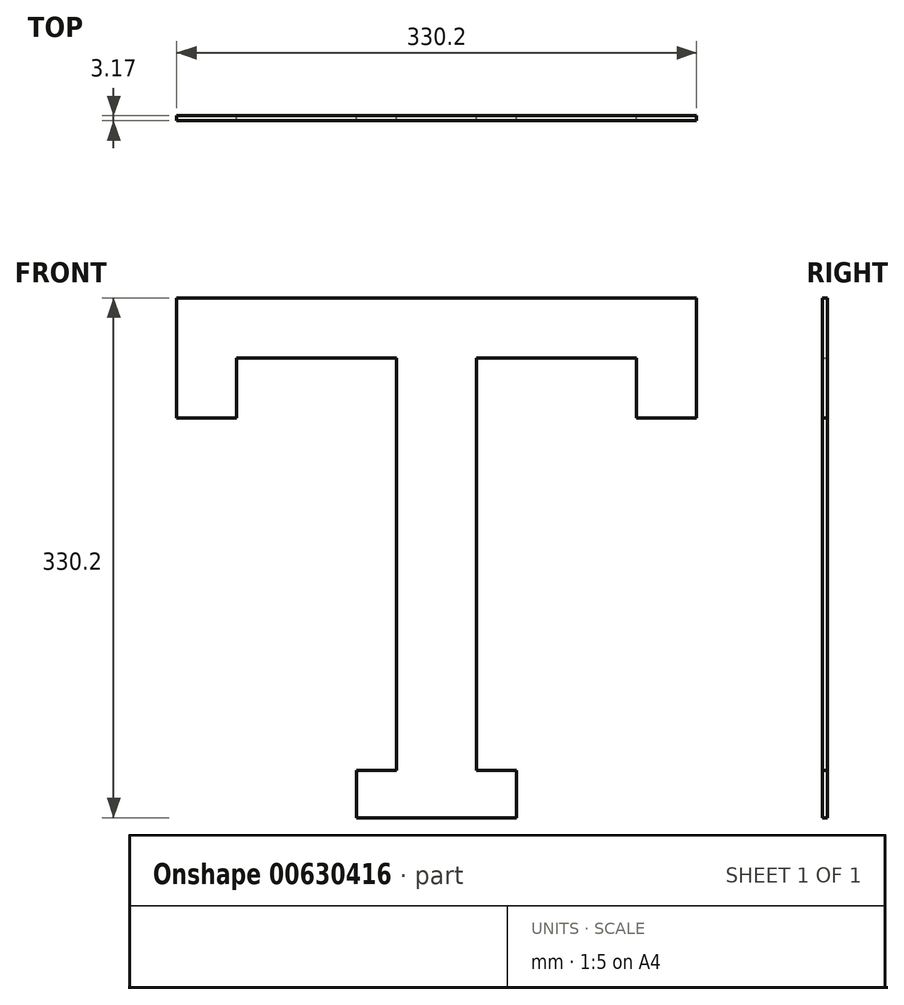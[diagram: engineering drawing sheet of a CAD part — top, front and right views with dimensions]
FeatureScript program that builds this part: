
annotation { "Feature Type Name" : "Feature", "Feature Type Description" : "" }
export const myFeature = defineFeature(function(context is Context, id is Id, definition is map)
    precondition{}
    {
        {
            var Q0;
            Q0=qCreatedBy(makeId("Front.planeOp"),FACE);
            var sketch = newSketch(context, id + "F0", { "sketchPlane" : qUnion([Q0])});
            skLineSegment(sketch, "E0.bottom", {"start": v(-25.4, 330.2) * mm, "end": v(0, 330.2) * mm});
            skLineSegment(sketch, "E0.top", {"start": v(-25.4, 0) * mm, "end": v(0, 0) * mm});
            skLineSegment(sketch, "E0.left", {"start": v(-25.4, 292.1) * mm, "end": v(-25.4, 30.02) * mm});
            skLineSegment(sketch, "E0.right", {"start": v(0, 330.2) * mm, "end": v(0, 0) * mm, "construction": true});
            skLineSegment(sketch, "E1.bottom", {"start": v(0, 330.2) * mm, "end": v(-165.1, 330.2) * mm});
            skLineSegment(sketch, "E1.top", {"start": v(-25.4, 292.1) * mm, "end": v(-127, 292.1) * mm});
            skLineSegment(sketch, "E1.left", {"start": v(0, 330.2) * mm, "end": v(0, 292.1) * mm});
            skLineSegment(sketch, "E1.right", {"start": v(-165.1, 330.2) * mm, "end": v(-165.1, 292.1) * mm});
            skLineSegment(sketch, "E2.bottom", {"start": v(-165.1, 330.2) * mm, "end": v(-127, 330.2) * mm});
            skLineSegment(sketch, "E2.top", {"start": v(-165.1, 254) * mm, "end": v(-127, 254) * mm});
            skLineSegment(sketch, "E2.left", {"start": v(-165.1, 330.2) * mm, "end": v(-165.1, 254) * mm});
            skLineSegment(sketch, "E2.right", {"start": v(-127, 292.1) * mm, "end": v(-127, 254) * mm});
            skLineSegment(sketch, "E3.bottom", {"start": v(0, 0) * mm, "end": v(-50.8, 0) * mm});
            skLineSegment(sketch, "E3.top", {"start": v(-25.4, 30.02) * mm, "end": v(-50.8, 30.02) * mm});
            skLineSegment(sketch, "E3.left", {"start": v(0, 0) * mm, "end": v(0, 30.02) * mm});
            skLineSegment(sketch, "E3.right", {"start": v(-50.8, 0) * mm, "end": v(-50.8, 30.02) * mm});
            skLineSegment(sketch, "E4.MirrorCS", {"start": v(0, 330.2) * mm, "end": v(165.1, 330.2) * mm});
            skLineSegment(sketch, "E5.MirrorCS", {"start": v(165.1, 330.2) * mm, "end": v(165.1, 254) * mm});
            skLineSegment(sketch, "E6.MirrorCS", {"start": v(165.1, 254) * mm, "end": v(127, 254) * mm});
            skLineSegment(sketch, "E7.MirrorCS", {"start": v(127, 292.1) * mm, "end": v(127, 254) * mm});
            skLineSegment(sketch, "E8.MirrorCS", {"start": v(25.4, 292.1) * mm, "end": v(127, 292.1) * mm});
            skLineSegment(sketch, "E9.MirrorCS", {"start": v(25.4, 292.1) * mm, "end": v(25.4, 30.02) * mm});
            skLineSegment(sketch, "E10.MirrorCS", {"start": v(25.4, 30.02) * mm, "end": v(50.8, 30.02) * mm});
            skLineSegment(sketch, "E11.MirrorCS", {"start": v(50.8, 0) * mm, "end": v(50.8, 30.02) * mm});
            skLineSegment(sketch, "E12.MirrorCS", {"start": v(0, 0) * mm, "end": v(50.8, 0) * mm});
            skSolve(sketch);
        }
        {
            var Q0;
            Q0=makeQuery(id+"F0.imprint","IMPRINT",FACE,{"disambiguationData":[TD([[makeQuery(id+"F0.imprint","IMPRINT",EDGE,{"derivedFrom":sQuery(id+"F0.wireOp",EDGE,"E0.left")}),1.0]])]});
            extrude(context, id + "F1", {"entities" : qUnion([Q0]), "depth" : 3.17 * mm, "offsetDistance" : 25.4 * mm});
        }
    });
